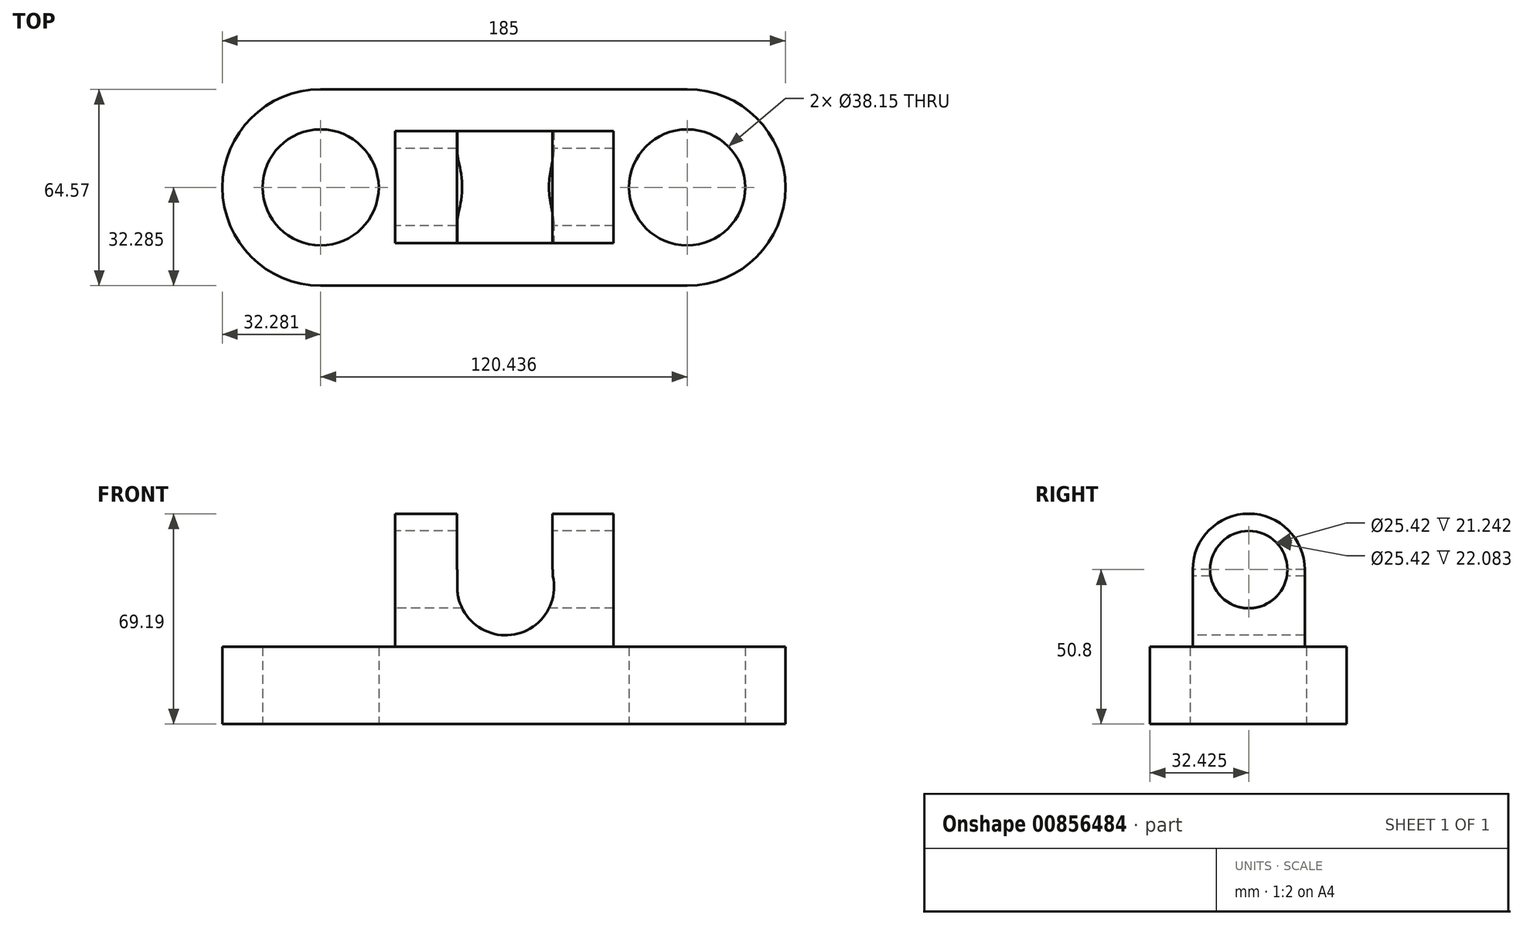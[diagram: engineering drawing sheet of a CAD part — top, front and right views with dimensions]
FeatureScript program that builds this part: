
annotation { "Feature Type Name" : "Feature", "Feature Type Description" : "" }
export const myFeature = defineFeature(function(context is Context, id is Id, definition is map)
    precondition{}
    {
        {
            var Q0;
            Q0=qCreatedBy(makeId("Top.planeOp"),FACE);
            var sketch = newSketch(context, id + "F0", { "sketchPlane" : qUnion([Q0])});
            skLineSegment(sketch, "E0.bottom", {"start": v(-60.78, 34.1) * mm, "end": v(59.66, 34.1) * mm});
            skLineSegment(sketch, "E0.top", {"start": v(-60.78, -30.46) * mm, "end": v(59.66, -30.46) * mm});
            skArc(sketch, "E1", {"start": v(-60.78, 34.1) * mm, "mid": v(-93.06, 1.82) * mm, "end": v(-60.78, -30.46) * mm});
            skArc(sketch, "E2", {"start": v(59.66, -30.46) * mm, "mid": v(91.94, 1.82) * mm, "end": v(59.66, 34.1) * mm});
            skCircle(sketch, "E3", {"center": v(-60.78, 1.82) * mm, "radius": 19.07 * mm});
            skCircle(sketch, "E4", {"center": v(59.66, 1.82) * mm, "radius": 19.07 * mm});
            skSolve(sketch);
        }
        {
            var Q0;
            Q0=makeQuery(id+"F0.imprint","IMPRINT",FACE,{"disambiguationData":[TD([[makeQuery(id+"F0.imprint","IMPRINT",EDGE,{"derivedFrom":sQuery(id+"F0.wireOp",EDGE,"E0.bottom")}),-1.0]])]});
            extrude(context, id + "F1", {"entities" : qUnion([Q0]), "depth" : 25.4 * mm, "offsetDistance" : 25.4 * mm});
        }
        {
            var Q0;
            Q0=makeQuery(id+"F1.opExtrude","CAP_FACE",FACE,{"disambiguationData":[OSD([sQuery(id+"F0.wireOp",EDGE,"E0.bottom"),sQuery(id+"F0.wireOp",EDGE,"E0.top"),sQuery(id+"F0.wireOp",EDGE,"E1"),sQuery(id+"F0.wireOp",EDGE,"E2"),sQuery(id+"F0.wireOp",EDGE,"E3"),sQuery(id+"F0.wireOp",EDGE,"E4")])],"isStart":false});
            var sketch = newSketch(context, id + "F2", { "sketchPlane" : qUnion([Q0])});
            skLineSegment(sketch, "E5.bottom", {"start": v(-36.36, 20.35) * mm, "end": v(35.51, 20.35) * mm});
            skLineSegment(sketch, "E5.top", {"start": v(-36.36, -16.42) * mm, "end": v(35.51, -16.42) * mm});
            skLineSegment(sketch, "E5.left", {"start": v(-36.36, 20.35) * mm, "end": v(-36.36, -16.42) * mm});
            skLineSegment(sketch, "E5.right", {"start": v(35.51, 20.35) * mm, "end": v(35.51, -16.42) * mm});
            skSolve(sketch);
        }
        {
            var Q0;
            Q0=makeQuery(id+"F2.imprint","IMPRINT",FACE,{"disambiguationData":[TD([[makeQuery(id+"F2.imprint","IMPRINT",EDGE,{"derivedFrom":sQuery(id+"F2.wireOp",EDGE,"E5.bottom")}),-1.0]])]});
            extrude(context, id + "F3", {"entities" : qUnion([Q0]), "operationType" : NewBodyOperationType.ADD, "depth" : 25.4 * mm, "offsetDistance" : 25.4 * mm});
        }
        {
            var Q0;
            Q0=makeQuery(id+"F3.opExtrude","SWEPT_FACE",FACE,{"disambiguationData":[OSD([sQuery(id+"F2.wireOp",EDGE,"E5.top")])]});
            var sketch = newSketch(context, id + "F4", { "sketchPlane" : qUnion([Q0])});
            skLineSegment(sketch, "E6.left", {"start": v(-15.92, 50.8) * mm, "end": v(-15.92, 45.15) * mm});
            skLineSegment(sketch, "E6.right", {"start": v(15.52, 76.2) * mm, "end": v(15.52, 45.15) * mm});
            skArc(sketch, "E7", {"start": v(-15.92, 45.15) * mm, "mid": v(1.8, 29.32) * mm, "end": v(15.52, 48.72) * mm});
            skSolve(sketch);
        }
        {
            var Q0;
            {var subQ0=sQuery(id+"F4.wireOp",EDGE,"E6.left");Q0=makeQuery(id+"F4.imprint","IMPRINT",FACE,{"disambiguationData":[TD([[makeQuery(id+"F4.imprint","IMPRINT",EDGE,{"derivedFrom":subQ0}),1.0]])]});}
            extrude(context, id + "F5", {"entities" : qUnion([Q0]), "operationType" : NewBodyOperationType.REMOVE, "oppositeDirection" : true, "depth" : 43.94 * mm, "offsetDistance" : 25.4 * mm});
        }
        {
            var Q0;
            Q0=makeQuery(id+"F3.opExtrude","SWEPT_FACE",FACE,{"disambiguationData":[OSD([sQuery(id+"F2.wireOp",EDGE,"E5.left")])]});
            var sketch = newSketch(context, id + "F6", { "sketchPlane" : qUnion([Q0])});
            skArc(sketch, "E8", {"start": v(16.42, 50.8) * mm, "mid": v(-1.97, 69.19) * mm, "end": v(-20.35, 50.8) * mm});
            skLineSegment(sketch, "E9.top", {"start": v(-20.35, 25.4) * mm, "end": v(16.42, 25.4) * mm});
            skLineSegment(sketch, "E9.left", {"start": v(-20.35, 50.8) * mm, "end": v(-20.35, 25.4) * mm});
            skLineSegment(sketch, "E9.right", {"start": v(16.42, 50.8) * mm, "end": v(16.42, 25.4) * mm});
            skSolve(sketch);
        }
        {
            var Q0;
            Q0=makeQuery(id+"F6.imprint","IMPRINT",FACE,{"disambiguationData":[TD([[makeQuery(id+"F6.imprint","IMPRINT",EDGE,{"derivedFrom":sQuery(id+"F6.wireOp",EDGE,"E8")}),1.0]])]});
            extrude(context, id + "F7", {"entities" : qUnion([Q0]), "operationType" : NewBodyOperationType.ADD, "oppositeDirection" : true, "depth" : 20.32 * mm, "offsetDistance" : 25.4 * mm});
        }
        {
            var Q0;
            Q0=makeQuery(id+"F3.opExtrude","SWEPT_FACE",FACE,{"disambiguationData":[OSD([sQuery(id+"F2.wireOp",EDGE,"E5.right")])]});
            var sketch = newSketch(context, id + "F8", { "sketchPlane" : qUnion([Q0])});
            skLineSegment(sketch, "E10.top", {"start": v(-16.42, 25.4) * mm, "end": v(20.35, 25.4) * mm});
            skLineSegment(sketch, "E10.left", {"start": v(-16.42, 50.8) * mm, "end": v(-16.42, 25.4) * mm});
            skLineSegment(sketch, "E10.right", {"start": v(20.35, 50.8) * mm, "end": v(20.35, 25.4) * mm});
            skArc(sketch, "E11", {"start": v(20.35, 50.8) * mm, "mid": v(1.97, 69.19) * mm, "end": v(-16.42, 50.8) * mm});
            skSolve(sketch);
        }
        {
            var Q0;
            Q0=makeQuery(id+"F8.imprint","IMPRINT",FACE,{"disambiguationData":[TD([[makeQuery(id+"F8.imprint","IMPRINT",EDGE,{"derivedFrom":sQuery(id+"F8.wireOp",EDGE,"E11")}),1.0]])]});
            extrude(context, id + "F9", {"entities" : qUnion([Q0]), "operationType" : NewBodyOperationType.ADD, "oppositeDirection" : true, "depth" : 20.07 * mm, "offsetDistance" : 25.4 * mm});
        }
        {
            var Q0;
            {var subQ0=sQuery(id+"F2.wireOp",EDGE,"E5.left");Q0=makeQuery(id+"F7.boolean.opBoolean","MERGE",FACE,{"derivedFrom":[makeQuery(id+"F3.opExtrude","SWEPT_FACE",FACE,{"disambiguationData":[OSD([subQ0])]}),makeQuery(id+"F7.opExtrude","CAP_FACE",FACE,{"disambiguationData":[OSD([subQ0,sQuery(id+"F6.wireOp",EDGE,"E8")])],"isStart":true})]});}
            var sketch = newSketch(context, id + "F10", { "sketchPlane" : qUnion([Q0])});
            skCircle(sketch, "E12", {"center": v(-1.97, 50.8) * mm, "radius": 12.7 * mm});
            skPoint(sketch, "E13.start.orphan", {"position": v(-1.97, 25.4) * mm});
            skPoint(sketch, "E14.start.orphan", {"position": v(-1.97, 69.19) * mm});
            skSolve(sketch);
        }
        {
            var Q0;
            Q0=makeQuery(id+"F10.imprint","IMPRINT",FACE,{"disambiguationData":[TD([[makeQuery(id+"F10.imprint","IMPRINT",EDGE,{"derivedFrom":sQuery(id+"F10.wireOp",EDGE,"E12")}),1.0]])]});
            extrude(context, id + "F11", {"entities" : qUnion([Q0]), "operationType" : NewBodyOperationType.REMOVE, "oppositeDirection" : true, "depth" : 88.65 * mm, "offsetDistance" : 25.4 * mm});
        }
    });
